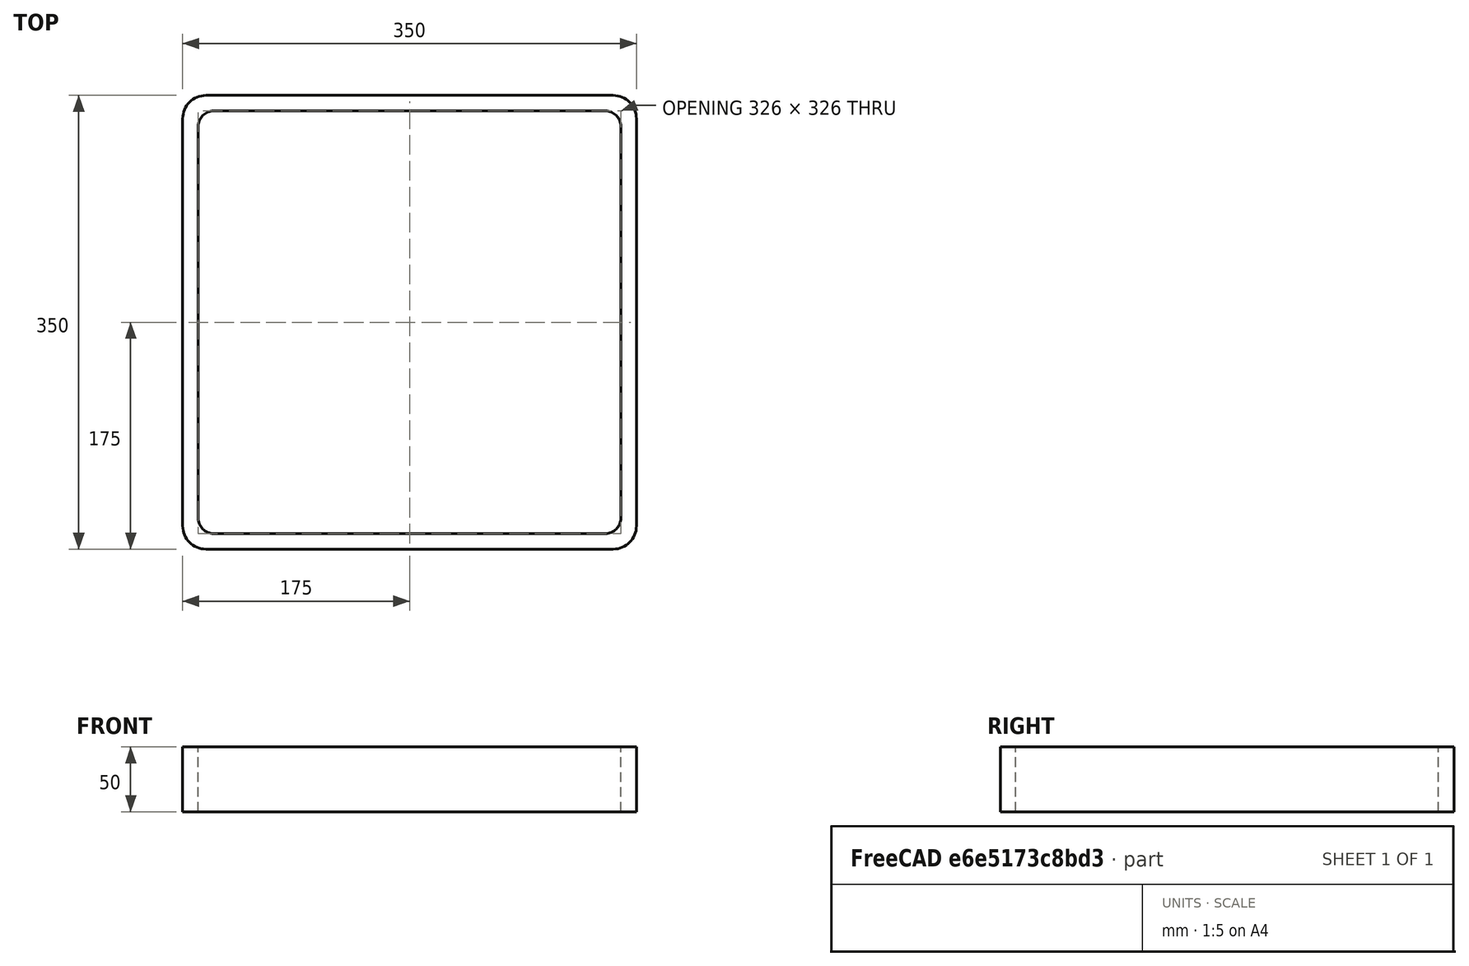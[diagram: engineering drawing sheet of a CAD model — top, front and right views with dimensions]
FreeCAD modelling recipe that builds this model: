
FCSTD DOCUMENT  (FreeCAD 0.15R4671 (Git))
Label: Square hollow section 350x350x12 EN10219 S235JRH
License: All rights reserved
LicenseURL: http://en.wikipedia.org/wiki/All_rights_reserved
objects: Sketcher::SketchObject×1, Part::Extrusion×1
note: 2 computed .brp shape members not serialized (recipe doc carries the construction recipe); baked Part::Feature solids carry a one-line shape summary decoded from their .brp

FEATURE [Sketcher::SketchObject] Sketch
  sketch-geometry (16):
    g0: LineSegment StartX=-151 StartY=163 StartZ=0 EndX=151 EndY=163 EndZ=0
    g1: LineSegment StartX=163 StartY=151 StartZ=0 EndX=163 EndY=-151 EndZ=0
    g2: LineSegment StartX=151 StartY=-163 StartZ=0 EndX=-151 EndY=-163 EndZ=0
    g3: LineSegment StartX=-163 StartY=-151 StartZ=0 EndX=-163 EndY=151 EndZ=0
    g4: LineSegment StartX=-157 StartY=175 StartZ=0 EndX=157 EndY=175 EndZ=0
    g5: LineSegment StartX=175 StartY=157 StartZ=0 EndX=175 EndY=-157 EndZ=0
    g6: LineSegment StartX=157 StartY=-175 StartZ=0 EndX=-157 EndY=-175 EndZ=0
    g7: LineSegment StartX=-175 StartY=-157 StartZ=0 EndX=-175 EndY=157 EndZ=0
    g8: ArcOfCircle CenterX=-151 CenterY=151 CenterZ=0 NormalX=0 NormalY=0 NormalZ=1 Radius=12 StartAngle=1.5708 EndAngle=3.14159
    g9: ArcOfCircle CenterX=151 CenterY=151 CenterZ=0 NormalX=0 NormalY=0 NormalZ=1 Radius=12 StartAngle=0 EndAngle=1.5708
    g10: ArcOfCircle CenterX=151 CenterY=-151 CenterZ=0 NormalX=0 NormalY=0 NormalZ=1 Radius=12 StartAngle=4.71239 EndAngle=6.28319
    g11: ArcOfCircle CenterX=-151 CenterY=-151 CenterZ=0 NormalX=0 NormalY=0 NormalZ=1 Radius=12 StartAngle=3.14159 EndAngle=4.71239
    g12: ArcOfCircle CenterX=157 CenterY=157 CenterZ=0 NormalX=0 NormalY=0 NormalZ=1 Radius=18 StartAngle=0 EndAngle=1.5708
    g13: ArcOfCircle CenterX=157 CenterY=-157 CenterZ=0 NormalX=0 NormalY=0 NormalZ=1 Radius=18 StartAngle=4.71239 EndAngle=6.28319
    g14: ArcOfCircle CenterX=-157 CenterY=-157 CenterZ=0 NormalX=0 NormalY=0 NormalZ=1 Radius=18 StartAngle=3.14159 EndAngle=4.71239
    g15: ArcOfCircle CenterX=-157 CenterY=157 CenterZ=0 NormalX=0 NormalY=0 NormalZ=1 Radius=18 StartAngle=1.5708 EndAngle=3.14159
  constraints (36):
    c: Horizontal(g2)
    c: Vertical(g3)
    c: Horizontal(g6)
    c: Vertical(g7)
    c: Tangent(g3,g8) = 1.5708
    c: Tangent(g0,g8) = 1.5708
    c: Tangent(g0,g9) = 1.5708
    c: Tangent(g1,g9) = 1.5708
    c: Tangent(g1,g10) = 1.5708
    c: Tangent(g2,g10) = 1.5708
    c: Tangent(g2,g11) = 1.5708
    c: Tangent(g3,g11) = 1.5708
    c: Tangent(g4,g12) = 1.5708
    c: Tangent(g5,g12) = 1.5708
    c: Tangent(g5,g13) = 1.5708
    c: Tangent(g6,g13) = 1.5708
    c: Tangent(g6,g14) = 1.5708
    c: Tangent(g7,g14) = 1.5708
    c: Tangent(g7,g15) = 1.5708
    c: Tangent(g4,g15) = 1.5708
    c: Equal(g9,g8)
    c: Equal(g9,g11)
    c: Equal(g9,g10)
    c: Equal(g12,g15)
    c: Equal(g12,g14)
    c: Equal(g12,g13)
    c: Symmetric(g4,g6,g-1)
    c: Symmetric(g7,g5,g-2)
    c: DistanceY(g4,g6) = -350
    c: DistanceX(g7,g5) = 350
    c: Symmetric(g3,g1,g-2)
    c: Symmetric(g0,g2,g-1)
    c: DistanceY(g0,g4) = 12
    c: DistanceX(g5,g1) = -12
    c: Radius(g9) = 12
    c: Radius(g12) = 18
FEATURE [Part::Extrusion] Extrude  label="Square hollow section 350x350x12 EN10219 S235JRH"
  Base = -> Sketch
  Dir = (0,0,50)
  Solid = true
